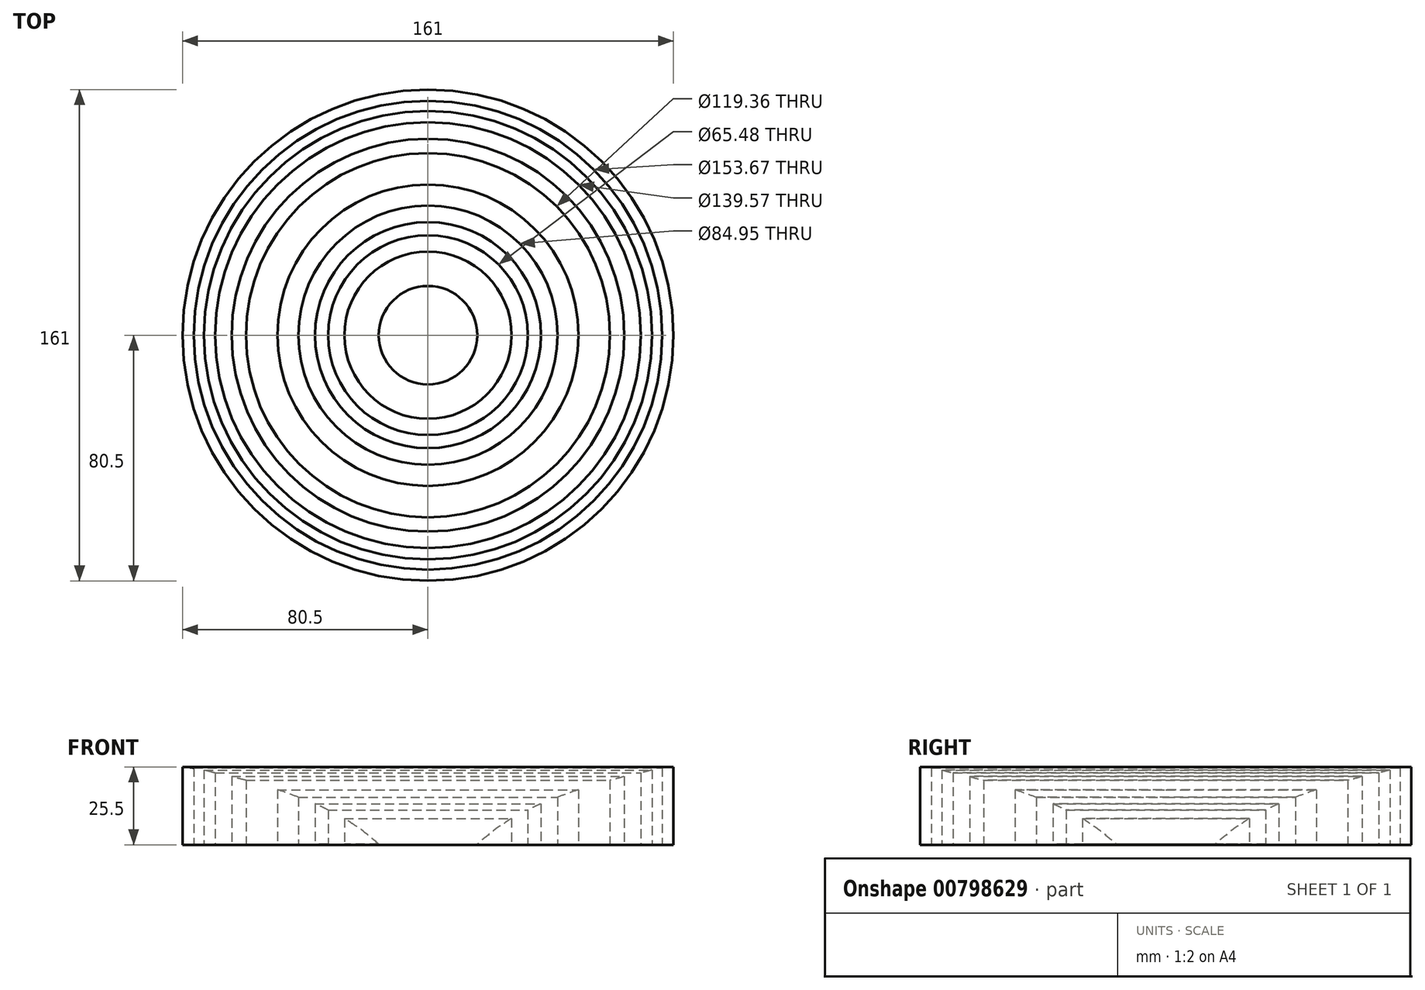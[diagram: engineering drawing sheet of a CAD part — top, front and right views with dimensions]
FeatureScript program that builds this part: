
annotation { "Feature Type Name" : "Feature", "Feature Type Description" : "" }
export const myFeature = defineFeature(function(context is Context, id is Id, definition is map)
    precondition{}
    {
        {
            var Q0;
            Q0=qCreatedBy(makeId("Front.planeOp"),FACE);
            var sketch = newSketch(context, id + "F0", { "sketchPlane" : qUnion([Q0])});
            skPoint(sketch, "E0", {"position": v(16.14, 1.56) * mm});
            skPoint(sketch, "E1", {"position": v(17.72, 2.9) * mm});
            skPoint(sketch, "E2", {"position": v(19.43, 4.3) * mm});
            skPoint(sketch, "E3", {"position": v(21.24, 5.78) * mm});
            skPoint(sketch, "E4", {"position": v(22.54, 6.75) * mm});
            skPoint(sketch, "E5", {"position": v(23.74, 7.59) * mm});
            skPoint(sketch, "E6", {"position": v(25.37, 8.65) * mm});
            skPoint(sketch, "E7", {"position": v(26.43, 9.4) * mm});
            skPoint(sketch, "E8", {"position": v(27.4, 10) * mm});
            skPoint(sketch, "E9", {"position": v(28.38, 10.55) * mm});
            skPoint(sketch, "E10", {"position": v(29.77, 11.25) * mm});
            skPoint(sketch, "E11", {"position": v(30.6, 11.76) * mm});
            skPoint(sketch, "E12", {"position": v(31.49, 12.08) * mm});
            skPoint(sketch, "E13", {"position": v(32.74, 12.73) * mm});
            skPoint(sketch, "E14", {"position": v(34.6, 13.61) * mm});
            skPoint(sketch, "E15", {"position": v(35.52, 14.12) * mm});
            skPoint(sketch, "E16", {"position": v(37.05, 14.82) * mm});
            skPoint(sketch, "E17", {"position": v(38.95, 15.51) * mm});
            skPoint(sketch, "E18", {"position": v(41, 16.35) * mm});
            skPoint(sketch, "E19", {"position": v(42.48, 16.9) * mm});
            skPoint(sketch, "E20", {"position": v(43.91, 17.42) * mm});
            skPoint(sketch, "E21", {"position": v(45.44, 18.07) * mm});
            skPoint(sketch, "E22", {"position": v(46.6, 18.48) * mm});
            skPoint(sketch, "E23", {"position": v(47.44, 18.71) * mm});
            skPoint(sketch, "E24", {"position": v(48.74, 19.36) * mm});
            skPoint(sketch, "E25", {"position": v(49.38, 19.46) * mm});
            skPoint(sketch, "E26", {"position": v(50.27, 19.78) * mm});
            skPoint(sketch, "E27", {"position": v(50.91, 19.83) * mm});
            skPoint(sketch, "E28", {"position": v(53.05, 20.66) * mm});
            skPoint(sketch, "E29", {"position": v(54.62, 20.99) * mm});
            skPoint(sketch, "E30", {"position": v(56.76, 21.36) * mm});
            skPoint(sketch, "E31", {"position": v(58.1, 22.15) * mm});
            skPoint(sketch, "E32", {"position": v(59.68, 22.42) * mm});
            skPoint(sketch, "E33", {"position": v(61.72, 22.98) * mm});
            skPoint(sketch, "E34", {"position": v(62.88, 23.17) * mm});
            skPoint(sketch, "E35", {"position": v(64.36, 23.72) * mm});
            skPoint(sketch, "E36", {"position": v(65.7, 24.1) * mm});
            skPoint(sketch, "E37", {"position": v(67.98, 24.46) * mm});
            skPoint(sketch, "E38", {"position": v(69.79, 24.83) * mm});
            skPoint(sketch, "E39", {"position": v(71.87, 25.44) * mm});
            skPoint(sketch, "E40", {"position": v(73.45, 25.72) * mm});
            skPoint(sketch, "E41", {"position": v(75.35, 26.32) * mm});
            skPoint(sketch, "E42", {"position": v(76.83, 26.6) * mm});
            skPoint(sketch, "E43", {"position": v(78.78, 26.83) * mm});
            skPoint(sketch, "E44", {"position": v(80.5, 27.38) * mm});
            skFitSpline(sketch, "E45", {"points": [v(16.14, 1.56) * mm, v(17.72, 2.9) * mm, v(19.43, 4.3) * mm, v(21.24, 5.78) * mm, v(22.54, 6.75) * mm, v(23.74, 7.59) * mm, v(25.37, 8.65) * mm, v(26.43, 9.4) * mm, v(29.77, 11.25) * mm, v(32.74, 12.73) * mm, v(35.52, 14.12) * mm, v(38.95, 15.51) * mm, v(42.48, 16.9) * mm, v(46.6, 18.48) * mm, v(50.91, 19.83) * mm, v(54.62, 20.99) * mm, v(58.1, 22.15) * mm, v(61.72, 22.98) * mm, v(64.36, 23.72) * mm, v(67.98, 24.46) * mm, v(71.87, 25.44) * mm, v(75.35, 26.32) * mm, v(78.78, 26.83) * mm, v(80.5, 26.83) * mm], "startDerivative": vector(42.75, 37.28) * mm, "endDerivative": vector(47.04, -2) * mm});
            skLineSegment(sketch, "E46", {"start": v(80.5, 26.83) * mm, "end": v(80.5, 1.35) * mm});
            skLineSegment(sketch, "E47", {"start": v(80.5, 1.35) * mm, "end": v(16.14, 1.56) * mm});
            skLineSegment(sketch, "E48", {"start": v(0, 1.54) * mm, "end": v(0, 32.24) * mm});
            skLineSegment(sketch, "E49", {"start": v(0, 1.54) * mm, "end": v(0.07, 1.54) * mm});
            skLineSegment(sketch, "E50", {"start": v(0.07, 1.54) * mm, "end": v(0, 32.24) * mm});
            skLineSegment(sketch, "E51", {"start": v(32.74, 12.73) * mm, "end": v(32.74, 1.56) * mm});
            skLineSegment(sketch, "E52", {"start": v(49.38, 19.46) * mm, "end": v(49.38, 1.45) * mm});
            skLineSegment(sketch, "E53", {"start": v(64.36, 23.72) * mm, "end": v(64.36, 1.4) * mm});
            skLineSegment(sketch, "E54", {"start": v(23.74, 7.59) * mm, "end": v(23.72, 0) * mm});
            skLineSegment(sketch, "E55", {"start": v(37.05, 14.82) * mm, "end": v(37.05, 1.49) * mm});
            skLineSegment(sketch, "E56", {"start": v(42.48, 16.9) * mm, "end": v(42.48, 1.47) * mm});
            skLineSegment(sketch, "E57", {"start": v(54.62, 20.99) * mm, "end": v(54.62, 1.43) * mm});
            skLineSegment(sketch, "E58", {"start": v(59.68, 22.42) * mm, "end": v(59.68, 1.42) * mm});
            skLineSegment(sketch, "E59", {"start": v(45.44, 18.07) * mm, "end": v(45.44, 1.46) * mm});
            skLineSegment(sketch, "E60", {"start": v(69.79, 24.83) * mm, "end": v(69.79, 1.39) * mm});
            skLineSegment(sketch, "E61", {"start": v(73.45, 25.72) * mm, "end": v(73.45, 1.37) * mm});
            skLineSegment(sketch, "E62", {"start": v(76.83, 26.6) * mm, "end": v(76.83, 1.36) * mm});
            skLineSegment(sketch, "E63", {"start": v(27.4, 10) * mm, "end": v(27.4, 1.52) * mm});
            skLineSegment(sketch, "E64", {"start": v(32.74, 12.73) * mm, "end": v(32.74, -1.63) * mm});
            skLineSegment(sketch, "E65", {"start": v(54.62, 20.99) * mm, "end": v(54.62, -5.2) * mm});
            skLineSegment(sketch, "E66", {"start": v(59.68, 22.42) * mm, "end": v(59.68, -0.92) * mm});
            skLineSegment(sketch, "E67", {"start": v(59.68, 20.72) * mm, "end": v(59.68, 23.49) * mm});
            skLineSegment(sketch, "E68", {"start": v(69.79, 22.68) * mm, "end": v(69.79, 27.13) * mm});
            skLineSegment(sketch, "E69", {"start": v(69.79, 27.13) * mm, "end": v(69.79, 0.64) * mm});
            skLineSegment(sketch, "E70", {"start": v(76.83, 20.52) * mm, "end": v(76.83, 30.9) * mm});
            skLineSegment(sketch, "E71", {"start": v(73.45, 21.35) * mm, "end": v(73.45, 28.52) * mm});
            skSolve(sketch);
        }
        {
            var Q0;
            Q0=qCreatedBy(makeId("Top.planeOp"),FACE);
            var sketch = newSketch(context, id + "F1", { "sketchPlane" : qUnion([Q0])});
            skCircle(sketch, "E72", {"center": v(0, 0) * mm, "radius": 82.55 * mm});
            skCircle(sketch, "E73", {"center": v(0, 0) * mm, "radius": 12.7 * mm});
            skSolve(sketch);
        }
        {
            var Q0;
            {var subQ0=sQuery(id+"F0.wireOp",EDGE,"E54");var subQ1=sQuery(id+"F0.wireOp",EDGE,"E45");var subQ2=makeQuery(id+"F0.imprint","INTERSECT",VERTEX,{"derivedFrom":[subQ1,subQ0]});Q0=makeQuery(id+"F0.imprint","IMPRINT",FACE,{"disambiguationData":[TD([[makeQuery(id+"F0.imprint","IMPRINT",EDGE,{"disambiguationData":[TD([[subQ2,-1.0]])],"derivedFrom":subQ1}),-1.0]])]});}
            var Q1;
            {var subQ0=sQuery(id+"F0.wireOp",EDGE,"E64");var subQ3=makeQuery(id+"F0.imprint","IMPRINT",VERTEX,{"derivedFrom":subQ0});Q1=makeQuery(id+"F0.imprint","IMPRINT",FACE,{"disambiguationData":[TD([[makeQuery(id+"F0.imprint","IMPRINT",EDGE,{"disambiguationData":[TD([[subQ3,1.0]])],"derivedFrom":subQ0}),1.0]])]});}
            var Q2;
            {var subQ0=sQuery(id+"F0.wireOp",EDGE,"E56");Q2=makeQuery(id+"F0.imprint","IMPRINT",FACE,{"disambiguationData":[TD([[makeQuery(id+"F0.imprint","IMPRINT",EDGE,{"derivedFrom":subQ0}),1.0]])]});}
            var Q3;
            {var subQ0=sQuery(id+"F0.wireOp",EDGE,"E65");var subQ1=sQuery(id+"F0.wireOp",EDGE,"E45");var subQ2=makeQuery(id+"F0.imprint","INTERSECT",VERTEX,{"derivedFrom":[subQ1,subQ0]});Q3=makeQuery(id+"F0.imprint","IMPRINT",FACE,{"disambiguationData":[TD([[makeQuery(id+"F0.imprint","IMPRINT",EDGE,{"disambiguationData":[TD([[subQ2,1.0]])],"derivedFrom":subQ1}),-1.0]])]});}
            var Q4;
            {var subQ0=sQuery(id+"F0.wireOp",EDGE,"E53");Q4=makeQuery(id+"F0.imprint","IMPRINT",FACE,{"disambiguationData":[TD([[makeQuery(id+"F0.imprint","IMPRINT",EDGE,{"derivedFrom":subQ0}),-1.0]])]});}
            var Q5;
            {var subQ0=sQuery(id+"F0.wireOp",EDGE,"E61");Q5=makeQuery(id+"F0.imprint","IMPRINT",FACE,{"disambiguationData":[TD([[makeQuery(id+"F0.imprint","IMPRINT",EDGE,{"derivedFrom":subQ0}),-1.0]])]});}
            var Q6;
            {var subQ1=sQuery(id+"F0.wireOp",EDGE,"E46");Q6=makeQuery(id+"F0.imprint","IMPRINT",FACE,{"disambiguationData":[TD([[makeQuery(id+"F0.imprint","IMPRINT",EDGE,{"derivedFrom":subQ1}),-1.0]])]});}
            var Q7;
            Q7=sQuery(id+"F0.wireOp",EDGE,"E48");
            revolve(context, id + "F2", {"surfaceOperationType" : NewSurfaceOperationType.NEW, "entities" : qUnion([Q0, Q1, Q2, Q3, Q4, Q5, Q6]), "axis" : qUnion([Q7]), "revolveType" : RevolveType.FULL});
        }
    });
